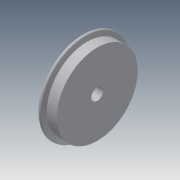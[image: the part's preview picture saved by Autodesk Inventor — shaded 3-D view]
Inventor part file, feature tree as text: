
AUTODESK INVENTOR PART (.ipt)
format: ipt  version: 2014 (Build 180170000, 170)  size: 117,760 bytes
history: native  units: in
note: dims shown in document units (in); Inventor stores cm internally (conversion verified against a paired STEP export)
features: sketch x2, revolve x1, extrude x1
ambient origin geometry x8: Origin, YZ Plane, XZ Plane, XY Plane, X Axis, Y Axis, Z Axis, Center Point
bodies: Solid1 (feature_tree)
feature tree (4):
  revolve  "Revolution1"  [1 undecoded]
  extrude  "Extrusion1"  Depth=1.0in
  sketch  "Sketch1"  dims[d0=1.0in d1=1.4375in]
  sketch  "Sketch2"  dims[d2=0.05in d3=0.46in d4=1.285in d5=0.14in d6=90.0deg d7=0.375in d8=1.0in d9=0.0in]
note: 1 required parameter value undecoded (feature->parameter linkage not recoverable at this tier; creation-order binding heuristic only, values carry confidence <= 0.55)
